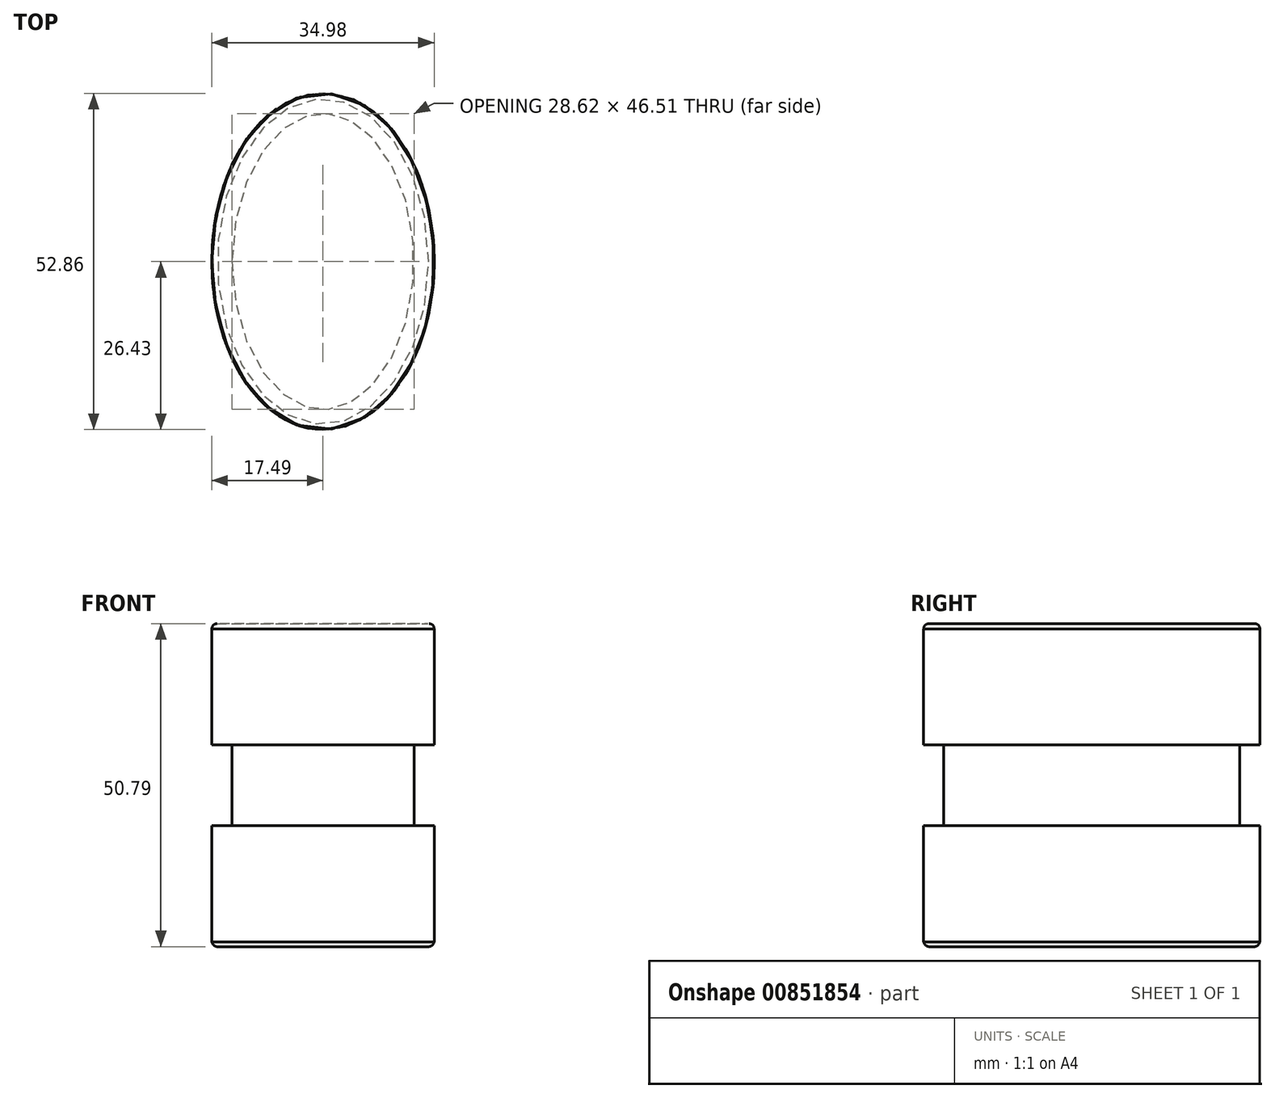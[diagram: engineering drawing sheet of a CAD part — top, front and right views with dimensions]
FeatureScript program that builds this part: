
annotation { "Feature Type Name" : "Feature", "Feature Type Description" : "" }
export const myFeature = defineFeature(function(context is Context, id is Id, definition is map)
    precondition{}
    {
        {
            var Q0;
            Q0=qCreatedBy(makeId("Top.planeOp"),FACE);
            var sketch = newSketch(context, id + "F0", { "sketchPlane" : qUnion([Q0])});
            skEllipse(sketch, "E0", {"center": v(0, 0) * mm, "majorRadius": 26.43 * mm, "minorRadius": 17.49 * mm, "majorAxis": v(0, -1)});
            skSolve(sketch);
        }
        {
            var Q0;
            Q0=qCreatedBy(makeId("Right.planeOp"),FACE);
            var sketch = newSketch(context, id + "F1", { "sketchPlane" : qUnion([Q0])});
            skLineSegment(sketch, "E1", {"start": v(0, 0) * mm, "end": v(0, 25.4) * mm});
            skLineSegment(sketch, "E2", {"start": v(0, 0) * mm, "end": v(0, -25.4) * mm});
            skSolve(sketch);
        }
        {
            var Q0;
            Q0=makeQuery(id+"F0.imprint","IMPRINT",FACE,{"disambiguationData":[TD([[makeQuery(id+"F0.imprint","IMPRINT",EDGE,{"derivedFrom":sQuery(id+"F0.wireOp",EDGE,"E0")}),1.0]])]});
            var Q1;
            Q1=sQuery(id+"F1.wireOp",EDGE,"E1");
            var Q2;
            Q2=sQuery(id+"F1.wireOp",EDGE,"E2");
            sweep(context, id + "F2", {"profiles" : qUnion([Q0]), "path" : qUnion([Q1, Q2])});
        }
        {
            var Q0;
            Q0=qCreatedBy(makeId("Front.planeOp"),FACE);
            var sketch = newSketch(context, id + "F3", { "sketchPlane" : qUnion([Q0])});
            skLineSegment(sketch, "E3.bottom", {"start": v(-17.49, 6.35) * mm, "end": v(-14.31, 6.35) * mm});
            skLineSegment(sketch, "E3.top", {"start": v(-17.49, -6.35) * mm, "end": v(-14.31, -6.35) * mm});
            skLineSegment(sketch, "E3.left", {"start": v(-17.49, 6.35) * mm, "end": v(-17.49, -6.35) * mm});
            skLineSegment(sketch, "E3.right", {"start": v(-14.31, 6.35) * mm, "end": v(-14.31, -6.35) * mm});
            skSolve(sketch);
        }
        {
            var Q0;
            Q0=makeQuery(id+"F3.imprint","IMPRINT",FACE,{"disambiguationData":[TD([[makeQuery(id+"F3.imprint","IMPRINT",EDGE,{"derivedFrom":sQuery(id+"F3.wireOp",EDGE,"E3.bottom")}),-1.0]])]});
            var Q1;
            Q1=makeQuery(id+"F2.opSweep","MID_CAP_EDGE",EDGE,{"disambiguationData":[OSD([sQuery(id+"F0.wireOp",EDGE,"E0"),sQuery(id+"F1.wireOp",VERTEX,"E2.start")])],"capPos":1.0});
            sweep(context, id + "F4", {"operationType" : NewBodyOperationType.REMOVE, "profiles" : qUnion([Q0]), "path" : qUnion([Q1])});
        }
        {
            var Q0;
            Q0=qCreatedBy(makeId("Front.planeOp"),FACE);
            var sketch = newSketch(context, id + "F5", { "sketchPlane" : qUnion([Q0])});
            skArc(sketch, "E4", {"start": v(16.6, -25.4) * mm, "mid": v(17.18, -25.17) * mm, "end": v(17.46, -24.62) * mm});
            skArc(sketch, "E5", {"start": v(16.6, -25.4) * mm, "mid": v(17.53, -25.56) * mm, "end": v(17.46, -24.62) * mm});
            skSolve(sketch);
        }
        {
            var Q0;
            Q0=makeQuery(id+"F5.imprint","IMPRINT",FACE,{"disambiguationData":[TD([[makeQuery(id+"F5.imprint","IMPRINT",EDGE,{"derivedFrom":sQuery(id+"F5.wireOp",EDGE,"E4")}),-1.0]])]});
            var Q1;
            Q1=makeQuery(id+"F2.opSweep","CAP_EDGE",EDGE,{"disambiguationData":[OSD([sQuery(id+"F0.wireOp",EDGE,"E0"),sQuery(id+"F1.wireOp",VERTEX,"E2.end")])],"isStart":true});
            sweep(context, id + "F6", {"operationType" : NewBodyOperationType.REMOVE, "profiles" : qUnion([Q0]), "path" : qUnion([Q1])});
        }
        {
            var Q0;
            Q0=qCreatedBy(makeId("Front.planeOp"),FACE);
            var sketch = newSketch(context, id + "F7", { "sketchPlane" : qUnion([Q0])});
            skArc(sketch, "E6", {"start": v(-16.68, 25.4) * mm, "mid": v(-17.26, 25.14) * mm, "end": v(-17.48, 24.54) * mm});
            skArc(sketch, "E7", {"start": v(-16.68, 25.4) * mm, "mid": v(-17.7, 25.55) * mm, "end": v(-17.48, 24.54) * mm});
            skSolve(sketch);
        }
        {
            var Q0;
            Q0=makeQuery(id+"F7.imprint","IMPRINT",FACE,{"disambiguationData":[TD([[makeQuery(id+"F7.imprint","IMPRINT",EDGE,{"derivedFrom":sQuery(id+"F7.wireOp",EDGE,"E6")}),-1.0]])]});
            var Q1;
            Q1=makeQuery(id+"F2.opSweep","CAP_EDGE",EDGE,{"disambiguationData":[OSD([sQuery(id+"F0.wireOp",EDGE,"E0"),sQuery(id+"F1.wireOp",VERTEX,"E1.end")])],"isStart":false});
            sweep(context, id + "F8", {"operationType" : NewBodyOperationType.REMOVE, "profiles" : qUnion([Q0]), "path" : qUnion([Q1])});
        }
    });
